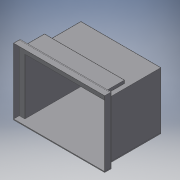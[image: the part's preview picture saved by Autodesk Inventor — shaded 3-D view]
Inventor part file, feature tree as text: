
AUTODESK INVENTOR PART (.ipt)
format: ipt  version: 2019 (Build 230136000, 136)  size: 206,848 bytes
history: native  units: in
note: dims shown in document units (in); Inventor stores cm internally (conversion verified against a paired STEP export)
features: extrude x10, sketch x10, projected_geometry x7
ambient origin geometry x8: Origin, YZ Plane, XZ Plane, XY Plane, X Axis, Y Axis, Z Axis, Center Point
bodies: Solid1 (feature_tree)
feature tree (27):
  extrude  "Extrusion1"  Depth=1.1811in
  extrude  "Extrusion2"  Depth=1.9685in
  extrude  "Extrusion3"  Depth=0.0315in
  extrude  "Extrusion4"  Depth=11.811in TaperAngle=0.0deg
  extrude  "Extrusion5"  Depth=1.1811in TaperAngle=0.0deg
  extrude  "Extrusion6"  Depth=0.3937in
  extrude  "Extrusion7"  Depth=0.0315in TaperAngle=0.0deg
  extrude  "Extrusion8"  Depth=3.937in TaperAngle=0.0deg
  extrude  "Extrusion9"  Depth=0.0315in TaperAngle=0.0deg
  extrude  "Extrusion10"  Depth=0.0315in TaperAngle=0.0deg
  sketch  "Sketch1"  dims[d0=0.3937in d1=1.1811in]
  sketch  "Sketch2"  dims[d2=1.1811in d3=1.9685in]
  projected_geometry  "Projected Loop1"
  sketch  "Sketch3"  dims[d4=0.1969in d5=0.0in d6=0.0315in]
  projected_geometry  "Projected Loop2"
  sketch  "Sketch4"  dims[d7=0.0315in d8=11.811in d9=0.0in]
  sketch  "Sketch5"  dims[d10=0.0315in d11=1.1811in d12=0.0in]
  projected_geometry  "Projected Loop3"
  sketch  "Sketch6"  dims[d13=0.5906in d14=0.3937in]
  projected_geometry  "Projected Loop4"
  sketch  "Sketch7"  dims[d15=1.1811in d16=0.0in d17=0.0315in d18=0.0in]
  projected_geometry  "Projected Loop5"
  sketch  "Sketch8"  dims[d19=0.0315in d20=3.937in d21=0.0in]
  projected_geometry  "Projected Loop6"
  sketch  "Sketch9"  dims[d22=0.1654in d23=0.0in d24=0.0315in d25=0.0in]
  sketch  "Sketch10"  dims[d26=0.3937in d27=0.0315in d28=0.0in d29=0.1654in d30=0.0in]
  projected_geometry  "Projected Loop7"
